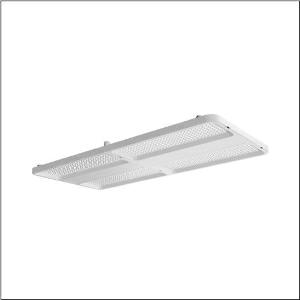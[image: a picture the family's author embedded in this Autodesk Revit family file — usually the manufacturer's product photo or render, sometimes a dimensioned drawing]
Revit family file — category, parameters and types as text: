
# Revit family: highbay_21_maxi_52hn11db4wda
name_source: partatom
category: Lighting Fixtures
units: mm (PartAtom-declared; Revit-internal decimal feet)

## family parameters
Cut with Voids When Loaded = No
Host = Face
Light Source = No
Part Type = Normal
Room Calculation Point = No
Round Connector Dimension = Use Diameter
Shared = No

## types (1)
- --- (1 x LED, 10140 lm, 55.2 W, 4000K)
    Apparent Load = 55 VA
    CIE Flux Codes = 89 97 99 100 100
    Color Rendering = 80
    Color Temperature = 4000K
    Default Elevation = 1800 mm
    Description = high bay luminaire Highbay 21 maxi; direct symmetric narrow distribution, light control with lens of PMMA; UGR ≤ 22 (X = 4H | Y = 8H | S = 0.25H | reflection values 70/50/20); luminous flux: 64.000lm; light colour: 840, colour temperature: 4000K, MacAdam ≤ 3 SDCM (initial), colour rendering: CRI > 80; luminous efficacy: 185,5lm/W; rated service life: 75.000h (L80) at AT= ta max; control: DALI 2; luminaire connection: terminal, 5-pole, max. 2.5mm² (cable entry for one cable, Ø 8.5..16mm); mains connection: 230..240V, AC/DC 0/50..60Hz; connected load: 345W; protection rating (complete): IP66; insulation class (complete): insulation class I (protective earthing); protection symbol: D; impact resistance: IK08; certification: CE, ENEC, VDE, UKCA; luminaire for central battery installations according to EN 60598-2-22, internal wiring halogen-free; luminaire LABS conformity tested according to VDMA 24364:2018-05; Suitable for use in the food industry according to the specifications of IFS-Food, HACCP and/or BRC; housing frame of high-performance plastic PA6, matt traffic white (RAL 9016); cover of PMMA; dimension (LxWxH): 946 x 442 x 72mm; permissible operating ambient temperature: -40..+50°C (reducing of maximum allowable ambient temperature of 5°C with ceiling mounting); packaging unit: 1 piece; (delivery without accessories; please order mounting accessories separately)
    Height = 72 mm  [stored 0.23622 ft]
    Lamp = 1 x LED
    Lamp Light Flux = 10140 lm
    Lamp Power = 55.2 W
    Lamp count = 1
    Length = 946 mm
    Luminous efficacy = 184 lm/W
    Manufacturer = Siteco
    ModVariant = No
    Model = 52HN11DB4WDA
    Mounting Place = Ceiling
    Mounting Type = Pendant
    Number of Poles = 1
    OnlyDefault = Yes
    Power Factor = 1
    Product Name = Highbay 21 maxi
    Product group = high bay luminaire
    ProductGroupID = 902
    Protection Class = Protection class I
    Protection Degree = IP 66
    RLX_Detail_Level = 1
    RLX_Emergency_Light_Flux = 0 lm
    RLX_Emergency_Type = 0
    RLX_Emergency_Type_DB = No
    RlxData = <blob elided: 128153 chars, md5=60845c0f>
    Socket = socket
    Standby Power = 0 W
    System Light Flux = 10140 lm
    System Power = 55 W
    Type Comments = : DC mode (central or group accumulator) initial emergency light level
    Type Image = l_1363244.jpg
    URL = http://relux.com
    VarID = @adj_017757
    Voltage = 0 V
    Weight = 0.00 kg
    Width = 442 mm

note: [stored X ft] marks values corroborated as IEEE doubles in the binary element streams (Revit-internal decimal feet)

## geometry (parser evidence)
native form markers: Blend x4, Sweep x10
no freeform markers — native parametric forms only
